# Revit family: Lighting-Industrial-GEWISS-SMART[4]HACCP_HIGHBAYS-LED_4M_DALI
name_source: partatom
category: Apparecchi per illuminazione
units: mm (PartAtom-declared; Revit-internal decimal feet)

## family parameters
Basato su piano di lavoro = Sì
Condiviso = No
Numero OmniClass = 23.80.70.00
Punto di calcolo locali = No
Quota connettore circolare = Usa diametro
Sempre verticale = No
Sorgente d'illuminazione = No
Taglio con vuoti quando caricato = No
Tipo di parte = Normale
Titolo OmniClass = Lighting

## types (12) — shared parameters
Application = Internal
Body = PA6 "Halogen Free" loaded fibreglass
Carico apparente = 194 VA
Catalogue = LIGHTING
Classification: = -
Classificazione = Lighting
Color Rendering Index = CRI-80
Colour = Grey RAL 7035
Colour : = Grey RAL 7035
Commenti sul wattaggio = 194W
Context = Lighting of logistical and industrial food productive premises
Control System = 1 x DALI DT6
Control System : = DALI
DIN 18032-3 certification = -
Device with reduced surface temperature = Yes
Distanza Sorg_Lum = 21 mm
Driver = Included
Driver Box = Built-in
Electrocod = 2444
Eletrical and lighting features = -
External screw = Stainless steel
Fixing = -
Gasket = anti-aging silicone
General information = -
Glow Wire Test : = 650 °C
IDF = 83bb5ed1-d9bc-4794-8449-086183d3a518
IDT = 8cae0c1428e746119892382860549084
IP degree = IP65
IPEA = -
Immagine tipo = GWL1371.jpg
Installationa and maintenance = -
Insulation class = I
LED Maintenance = Non-replaceable
Lampada = LED
Larghezza = 504 mm  [stored 1.65354 ft]
Lifetime = L90B10 (Tq+25°C) = 100.000 h - L90B10 (Tq+50°C) = 50.000 h
Locking Hook = -
Luminaire = LED Industrial ReflectorÂ
Lunghezza = 700 mm  [stored 2.29659 ft]
Materials = -
Maximum surface exposed to the wind : = 0,350 m²
Mouting and installation = Ceiling - Wallmounting - Suspension
Operating temperature : = -30 +50 °C
Optic Maintenance = Non-replaceable
Optic and illuminating features = -
Overvoltage protection = DM 6 kV / CM 10 kV
Photobiological Risk Class = RG0
Produttore = GEWISS S.p.A.
Prospetto di default = 1219 mm
Rated frequency (Hz) = 50/60 Hz
Shield type = PMMA
Shock resistance = IK07
Spessore plafoniera = 40 mm  [stored 0.131234 ft]
Standard Deviation Colour Matching = SDCM = 3
Standard- = EN 60598-1 ; EN 60598-2-1 ; EN 60598-2-24
Standards and approvals = -
Stocking temperature = -40 +70 °C
Supply voltage = 220 - 240 V
System power = 253W
Technical sheet = https://www.gewiss.com
Tilt- = With bracket accessory
Type of light source = LED - Not replaceable
URL = https://www.gewiss.com
Unique digital code (Datamatrix) = Datamatrix
Version file RFA = 20.11
Voltaggio = 230 V
Warranty = 5 years
Weight (kg): = 13,5
Wiring = With GW connect watertight connector

## per-type parameters (varying)
| type | Colour temperature | Descrizione | Efficiency (lm/W) | Lumen output (lm) | Modello | Optic | Optic : | SEO | Unified Glare Rating |
| GWS4421HA857 - SMART4HB 4M ST.AL.DALI HACCP ARR.57K | 5700K | SMART[4]HB 4M ST.AL.DALI HACCP ARR.57K | 144 | 36400 | GWS4421HA857 | Array | Metallized polycarbonate reflector |  | UGR - 25 |
| GWS4421HH857 - SMART4HB 4M ST.AL.DALI HACCP 60° 57K | 5700K | SMART[4]HB 4M ST.AL.DALI HACCP 60° 57K | 143 | 36100 | GWS4421HH857 | 60° | Metallic PC reflector and PMMA lenses |  | UGR - 22 |
| GWS4421HP857 - SMART4HB 4M ST.AL.DALI HACCP 90° 57K | 5700K | SMART[4]HB 4M ST.AL.DALI HACCP 90° 57K | 143 | 36100 | GWS4421HP857 | 90° | Metallic PC reflector and PMMA lenses |  | UGR - 22 |
| GWS4421HF857 - SMART4HB 4M ST.AL.DALI HACCP 30° 57K | 5700K | SMART[4]HB 4M ST.AL.DALI HACCP 30° 57K | 141 | 35700 | GWS4421HF857 | 30° | Metallic PC reflector and PMMA lenses |  | UGR - 19 |
| GWS4421HC840 - SMART4HB 4M ST.AL.DALI HACCP ASI.40K | 4000K | SMART[4]HB 4M ST.AL.DALI HACCP ASI.40K | 130 | 33000 | GWS4421HC840 | Asymmetrical | Metallic PC reflector and PMMA lenses | High bay | - |
| GWS4421HC857 - SMART4HB 4M ST.AL.DALI HACCP ASI.57K | 5700K | SMART[4]HB 4M ST.AL.DALI HACCP ASI.57K | 130 | 33000 | GWS4421HC857 | Asymmetrical | Metallic PC reflector and PMMA lenses | High bay | - |
| GWS4421HP840 - SMART4HB 4M ST.AL.DALI HACCP 90° 40K | 4000K | SMART[4]HB 4M ST.AL.DALI HACCP 90° 40K | 143 | 36100 | GWS4421HP840 | 90° | Metallic PC reflector and PMMA lenses |  | UGR - 22 |
| GWS4421HF840 - SMART4HB 4M ST.AL.DALI HACCP 30° 40K | 4000K | SMART[4]HB 4M ST.AL.DALI HACCP 30° 40K | 141 | 35700 | GWS4421HF840 | 30° | Metallic PC reflector and PMMA lenses |  | UGR - 19 |
| GWS4421HA840 - SMART4HB 4M ST.AL.DALI HACCP ARR.40K | 4000K | SMART[4]HB 4M ST.AL.DALI HACCP ARR.40K | 144 | 36400 | GWS4421HA840 | Array | Metallized polycarbonate reflector |  | UGR - 25 |
| GWS4421HQ840 - SMART4HB 4M ST.AL.DALI HACCP ELL.40K | 4000K | SMART[4]HB 4M ST.AL.DALI HACCP ELL.40K | 128 | 32500 | GWS4421HQ840 | Elliptical | Metallic PC reflector and PMMA lenses | High bay | - |
| GWS4421HH840 - SMART4HB 4M ST.AL.DALI HACCP 60° 40K | 4000K | SMART[4]HB 4M ST.AL.DALI HACCP 60° 40K | 143 | 36100 | GWS4421HH840 | 60° | Metallic PC reflector and PMMA lenses |  | UGR - 22 |
| GWS4421HQ857 - SMART4HB 4M ST.AL.DALI HACCP ELL.57K | 5700K | SMART[4]HB 4M ST.AL.DALI HACCP ELL.57K | 128 | 32500 | GWS4421HQ857 | Elliptical | Metallic PC reflector and PMMA lenses | High bay | - |

note: [stored X ft] marks values corroborated as IEEE doubles in the binary element streams (Revit-internal decimal feet)

## geometry (parser evidence)
native form markers: Sweep x1
no freeform markers — native parametric forms only
